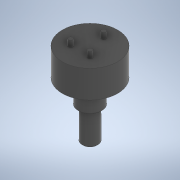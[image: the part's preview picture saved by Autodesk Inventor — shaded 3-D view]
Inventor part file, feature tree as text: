
AUTODESK INVENTOR PART (.ipt)
format: ipt  version: 2020 (Build 240168000, 168)  size: 171,008 bytes
history: native  units: in
note: dims shown in document units (in); Inventor stores cm internally (conversion verified against a paired STEP export)
features: sketch x4, extrude x3, revolve x1, chamfer x1
ambient origin geometry x8: Origin, YZ Plane, XZ Plane, XY Plane, X Axis, Y Axis, Z Axis, Center Point
bodies: Solid1 (feature_tree)
feature tree (9):
  revolve  "Revolution1"  [1 undecoded]
  chamfer  "Chamfer1"  Distance=0.203in
  extrude  "Extrusion1"  Depth=0.435in
  extrude  "Extrusion2"  Depth=0.4375in
  extrude  "Extrusion3"  Depth=0.098in
  sketch  "Sketch1"  dims[d0=0.875in d1=0.375in]
  sketch  "Sketch2"  dims[d2=0.059in]
  sketch  "Sketch3"  dims[d3=0.033in]
  sketch  "Sketch4"  dims[d4=0.1249in d5=0.203in d6=0.435in d7=0.4375in d8=0.1875in d9=90.0deg d10=0.0156in d11=0.125in d12=45.0deg d13=0.062in d14=0.29in d15=0.062in d16=0.0in d18=0.216in d19=0.375in d20=0.0in d21=0.435in d22=0.308in d23=0.07in d24=0.098in d25=0.0in]
note: 1 required parameter value undecoded (feature->parameter linkage not recoverable at this tier; creation-order binding heuristic only, values carry confidence <= 0.55)
